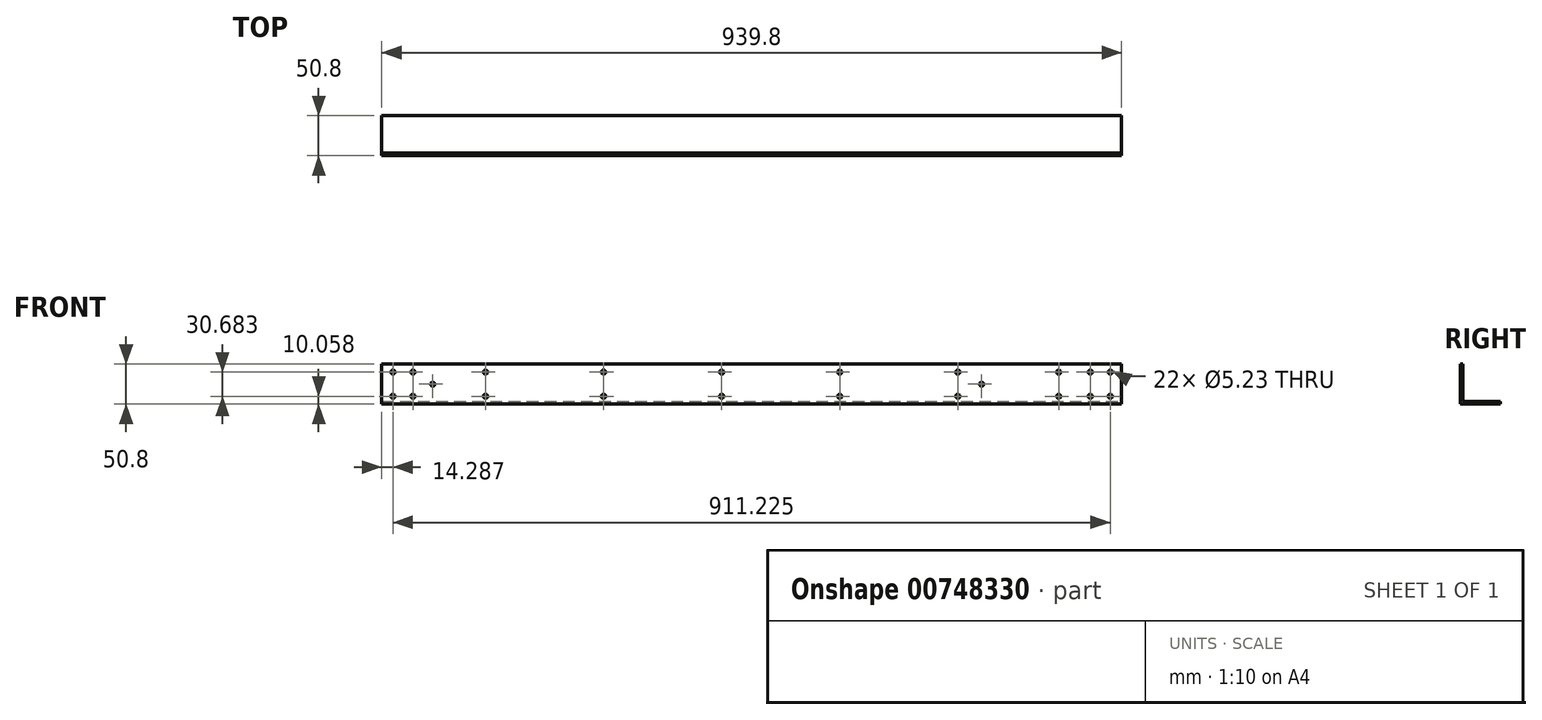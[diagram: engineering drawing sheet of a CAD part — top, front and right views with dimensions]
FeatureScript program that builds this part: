
annotation { "Feature Type Name" : "Feature", "Feature Type Description" : "" }
export const myFeature = defineFeature(function(context is Context, id is Id, definition is map)
    precondition{}
    {
        {
            var Q0;
            Q0=qCreatedBy(makeId("Right.planeOp"),FACE);
            var sketch = newSketch(context, id + "F0", { "sketchPlane" : qUnion([Q0])});
            skLineSegment(sketch, "E0", {"start": v(0, 0) * mm, "end": v(0, -44.45) * mm});
            skLineSegment(sketch, "E1", {"start": v(3.18, -47.62) * mm, "end": v(47.63, -47.62) * mm});
            skLineSegment(sketch, "E2.0", {"start": v(-3.18, -50.8) * mm, "end": v(47.63, -50.8) * mm});
            skLineSegment(sketch, "E2.1", {"start": v(-3.17, 0) * mm, "end": v(-3.18, -50.8) * mm});
            skLineSegment(sketch, "E3", {"start": v(-3.18, 0) * mm, "end": v(0, 0) * mm});
            skLineSegment(sketch, "E4", {"start": v(47.63, -47.62) * mm, "end": v(47.63, -50.8) * mm});
            skPoint(sketch, "E5.visualSharp", {"position": v(0, -47.63) * mm});
            skArc(sketch, "E5.filletArc", {"start": v(0, -44.45) * mm, "mid": v(0.93, -46.7) * mm, "end": v(3.18, -47.63) * mm});
            skSolve(sketch);
        }
        {
            var Q0;
            Q0=makeQuery(id+"F0.imprint","IMPRINT",FACE,{"disambiguationData":[TD([[makeQuery(id+"F0.imprint","IMPRINT",EDGE,{"derivedFrom":sQuery(id+"F0.wireOp",EDGE,"E0")}),-1.0]])]});
            extrude(context, id + "F1", {"entities" : qUnion([Q0]), "oppositeDirection" : true, "depth" : 939.8 * mm, "offsetDistance" : 25.4 * mm});
        }
        {
            var Q0;
            Q0=makeQuery(id+"F1.opExtrude","SWEPT_FACE",FACE,{"disambiguationData":[OSD([sQuery(id+"F0.wireOp",EDGE,"E2.1")])]});
            var sketch = newSketch(context, id + "F2", { "sketchPlane" : qUnion([Q0])});
            skLineSegment(sketch, "E6", {"start": v(0, -25.4) * mm, "end": v(-939.8, -25.4) * mm, "construction": true});
            skLineSegment(sketch, "E7", {"start": v(-508, -50.8) * mm, "end": v(-508, 0) * mm, "construction": true});
            skLineSegment(sketch, "E8", {"start": v(-14.29, -50.8) * mm, "end": v(-14.29, 0) * mm, "construction": true});
            skCircle(sketch, "E9", {"center": v(-14.29, -40.74) * mm, "radius": 2.62 * mm});
            skCircle(sketch, "E10", {"center": v(-14.29, -10.06) * mm, "radius": 2.62 * mm});
            skLineSegment(sketch, "E11", {"start": v(-925.51, 0) * mm, "end": v(-925.51, -50.8) * mm, "construction": true});
            skCircle(sketch, "E12", {"center": v(-925.51, -40.74) * mm, "radius": 2.62 * mm});
            skCircle(sketch, "E13", {"center": v(-925.51, -10.06) * mm, "radius": 2.62 * mm});
            skLineSegment(sketch, "E14.0", {"start": v(-63.5, -10.06) * mm, "end": v(-850.9, -10.06) * mm, "construction": true});
            skLineSegment(sketch, "E15.0", {"start": v(-63.5, -40.74) * mm, "end": v(-850.9, -40.74) * mm, "construction": true});
            skCircle(sketch, "E16", {"center": v(-508, -10.06) * mm, "radius": 2.62 * mm});
            skCircle(sketch, "E17", {"center": v(-508, -40.74) * mm, "radius": 2.62 * mm});
            skLineSegment(sketch, "E18.0", {"start": v(-177.8, -50.8) * mm, "end": v(-177.8, 0) * mm, "construction": true});
            skCircle(sketch, "E19", {"center": v(-875.03, -25.4) * mm, "radius": 2.62 * mm});
            skCircle(sketch, "E20", {"center": v(-177.8, -25.4) * mm, "radius": 2.62 * mm});
            skLineSegment(sketch, "E21", {"start": v(-39.69, -50.8) * mm, "end": v(-39.69, 0) * mm, "construction": true});
            skCircle(sketch, "E22", {"center": v(-39.69, -40.74) * mm, "radius": 2.62 * mm});
            skCircle(sketch, "E23", {"center": v(-39.69, -10.06) * mm, "radius": 2.62 * mm});
            skLineSegment(sketch, "E24", {"start": v(-900.11, -50.8) * mm, "end": v(-900.11, 0) * mm, "construction": true});
            skCircle(sketch, "E25", {"center": v(-900.11, -10.06) * mm, "radius": 2.62 * mm});
            skCircle(sketch, "E26", {"center": v(-900.11, -40.74) * mm, "radius": 2.62 * mm});
            skLineSegment(sketch, "E27", {"start": v(-79.84, -50.8) * mm, "end": v(-79.84, 0) * mm, "construction": true});
            skCircle(sketch, "E28", {"center": v(-79.84, -40.74) * mm, "radius": 2.62 * mm});
            skCircle(sketch, "E29", {"center": v(-79.84, -10.06) * mm, "radius": 2.62 * mm});
            skLineSegment(sketch, "E30", {"start": v(-875.03, 0) * mm, "end": v(-875.03, -50.8) * mm, "construction": true});
            skLineSegment(sketch, "E31.0", {"start": v(-358, -50.8) * mm, "end": v(-358, 0) * mm, "construction": true});
            skLineSegment(sketch, "E32.0", {"start": v(-208, -50.8) * mm, "end": v(-208, 0) * mm, "construction": true});
            skLineSegment(sketch, "E33.0", {"start": v(-658, -50.8) * mm, "end": v(-658, 0) * mm, "construction": true});
            skLineSegment(sketch, "E34.0", {"start": v(-808, -50.8) * mm, "end": v(-808, 0) * mm, "construction": true});
            skCircle(sketch, "E35", {"center": v(-808, -10.06) * mm, "radius": 2.62 * mm});
            skCircle(sketch, "E36", {"center": v(-808, -40.74) * mm, "radius": 2.62 * mm});
            skCircle(sketch, "E37", {"center": v(-658, -10.06) * mm, "radius": 2.62 * mm});
            skCircle(sketch, "E38", {"center": v(-658, -40.74) * mm, "radius": 2.62 * mm});
            skCircle(sketch, "E39", {"center": v(-358, -10.06) * mm, "radius": 2.62 * mm});
            skCircle(sketch, "E40", {"center": v(-358, -40.74) * mm, "radius": 2.62 * mm});
            skCircle(sketch, "E41", {"center": v(-208, -10.06) * mm, "radius": 2.62 * mm});
            skCircle(sketch, "E42", {"center": v(-208, -40.74) * mm, "radius": 2.62 * mm});
            skSolve(sketch);
        }
        {
            var Q0;
            Q0 = qSketchRegion(id + "F2", true);
            extrude(context, id + "F3", {"entities" : qUnion([Q0]), "operationType" : NewBodyOperationType.REMOVE, "endBound" : BoundingType.THROUGH_ALL, "oppositeDirection" : true, "depth" : 25.4 * mm, "offsetDistance" : 25.4 * mm});
        }
    });
